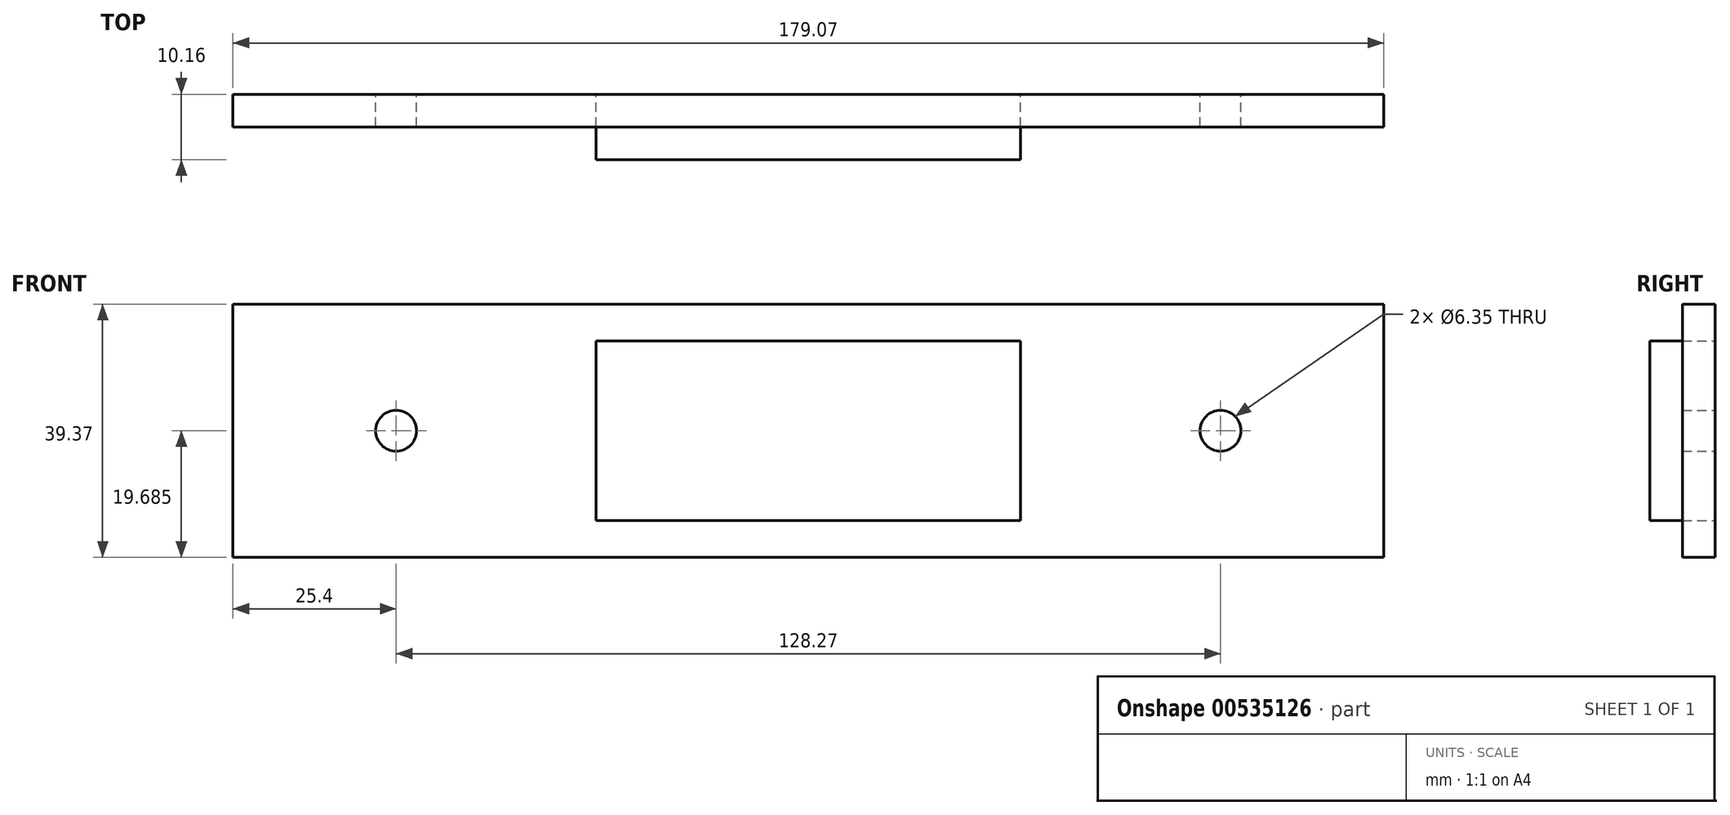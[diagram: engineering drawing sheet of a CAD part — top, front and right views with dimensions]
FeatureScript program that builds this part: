
annotation { "Feature Type Name" : "Feature", "Feature Type Description" : "" }
export const myFeature = defineFeature(function(context is Context, id is Id, definition is map)
    precondition{}
    {
        {
            var Q0;
            Q0=qCreatedBy(makeId("Front.planeOp"),FACE);
            var sketch = newSketch(context, id + "F0", { "sketchPlane" : qUnion([Q0])});
            skLineSegment(sketch, "E0.bottom", {"start": v(0, 0) * mm, "end": v(179.07, 0) * mm});
            skLineSegment(sketch, "E0.top", {"start": v(0, 39.37) * mm, "end": v(179.07, 39.37) * mm});
            skLineSegment(sketch, "E0.left", {"start": v(0, 0) * mm, "end": v(0, 39.37) * mm});
            skLineSegment(sketch, "E0.right", {"start": v(179.07, 0) * mm, "end": v(179.07, 39.37) * mm});
            skLineSegment(sketch, "E1.bottom", {"start": v(56.52, 33.66) * mm, "end": v(122.56, 33.66) * mm});
            skLineSegment(sketch, "E1.top", {"start": v(56.52, 5.71) * mm, "end": v(122.56, 5.71) * mm});
            skLineSegment(sketch, "E1.left", {"start": v(56.52, 33.66) * mm, "end": v(56.52, 5.71) * mm});
            skLineSegment(sketch, "E1.right", {"start": v(122.56, 33.66) * mm, "end": v(122.56, 5.71) * mm});
            skLineSegment(sketch, "E2", {"start": v(89.54, 33.66) * mm, "end": v(89.54, 5.71) * mm, "construction": true});
            skLineSegment(sketch, "E3", {"start": v(56.52, 19.69) * mm, "end": v(122.56, 19.69) * mm, "construction": true});
            skCircle(sketch, "E4", {"center": v(25.4, 19.69) * mm, "radius": 3.18 * mm});
            skPoint(sketch, "E4.centerSnap0", {"position": v(0, 19.69) * mm});
            skCircle(sketch, "E5", {"center": v(153.67, 19.69) * mm, "radius": 3.18 * mm});
            skLineSegment(sketch, "E6", {"start": v(0, 19.69) * mm, "end": v(50.8, 19.69) * mm, "construction": true});
            skLineSegment(sketch, "E7", {"start": v(179.07, 19.69) * mm, "end": v(128.27, 19.69) * mm, "construction": true});
            skSolve(sketch);
        }
        {
            var Q0;
            Q0=qSketchRegion(id+"F0",true);
            var Q1;
            Q1=makeQuery(id+"F0.imprint","IMPRINT",FACE,{"disambiguationData":[TD([[makeQuery(id+"F0.imprint","IMPRINT",EDGE,{"derivedFrom":sQuery(id+"F0.wireOp",EDGE,"E1.bottom")}),-1.0]])]});
            extrude(context, id + "F1", {"entities" : qUnion([Q0, Q1]), "depth" : 5.08 * mm});
        }
        {
            var Q0;
            Q0=makeQuery(id+"F0.imprint","IMPRINT",FACE,{"disambiguationData":[TD([[makeQuery(id+"F0.imprint","IMPRINT",EDGE,{"derivedFrom":sQuery(id+"F0.wireOp",EDGE,"E1.bottom")}),-1.0]])]});
            extrude(context, id + "F2", {"entities" : qUnion([Q0]), "depth" : 10.16 * mm});
        }
    });
